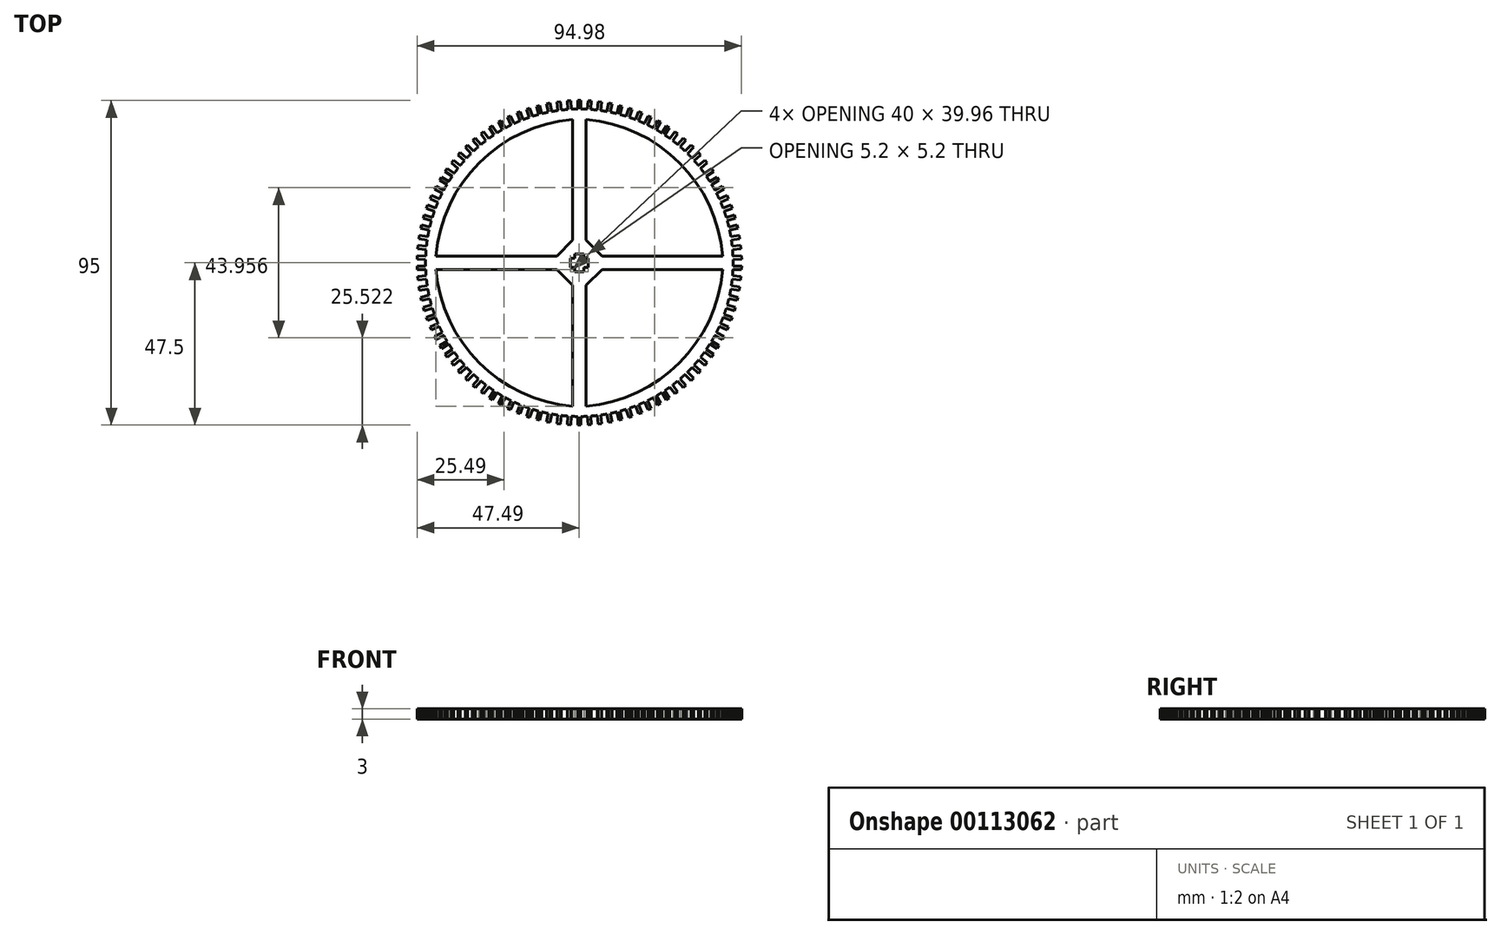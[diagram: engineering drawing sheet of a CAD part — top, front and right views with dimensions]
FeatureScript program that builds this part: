
annotation { "Feature Type Name" : "Feature", "Feature Type Description" : "" }
export const myFeature = defineFeature(function(context is Context, id is Id, definition is map)
    precondition{}
    {
        {
            var Q0;
            Q0=qCreatedBy(makeId("Top.planeOp"),FACE);
            var sketch = newSketch(context, id + "F0", { "sketchPlane" : qUnion([Q0])});
            skCircle(sketch, "E0", {"center": v(0, 0) * mm, "radius": 45 * mm});
            skLineSegment(sketch, "E1", {"start": v(0, 2.6) * mm, "end": v(1.3, 2.6) * mm});
            skLineSegment(sketch, "E2", {"start": v(1.3, 2.6) * mm, "end": v(1.3, 1.3) * mm});
            skLineSegment(sketch, "E3", {"start": v(1.3, 1.3) * mm, "end": v(2.6, 1.3) * mm});
            skLineSegment(sketch, "E4", {"start": v(2.6, 1.3) * mm, "end": v(2.6, 0) * mm});
            skLineSegment(sketch, "E5.MirrorCS", {"start": v(0, 2.6) * mm, "end": v(-1.3, 2.6) * mm});
            skLineSegment(sketch, "E6.MirrorCS", {"start": v(-1.3, 2.6) * mm, "end": v(-1.3, 1.3) * mm});
            skLineSegment(sketch, "E7.MirrorCS", {"start": v(-1.3, 1.3) * mm, "end": v(-2.6, 1.3) * mm});
            skLineSegment(sketch, "E8.MirrorCS", {"start": v(-2.6, 1.3) * mm, "end": v(-2.6, 0) * mm});
            skLineSegment(sketch, "E9", {"start": v(0, 45) * mm, "end": v(0, 47.5) * mm});
            skLineSegment(sketch, "E10", {"start": v(0, 47.5) * mm, "end": v(0.5, 47.5) * mm});
            skLineSegment(sketch, "E11", {"start": v(0.5, 47.5) * mm, "end": v(-0.5, 47.5) * mm});
            skLineSegment(sketch, "E12", {"start": v(-0.5, 47.5) * mm, "end": v(-0.5, 45) * mm});
            skLineSegment(sketch, "E13", {"start": v(0.5, 47.5) * mm, "end": v(0.5, 45) * mm});
            skLineSegment(sketch, "E14.1.0", {"start": v(-3.54, 47.37) * mm, "end": v(-3.38, 44.87) * mm});
            skLineSegment(sketch, "E14.1.1", {"start": v(-2.54, 47.43) * mm, "end": v(-3.54, 47.37) * mm});
            skLineSegment(sketch, "E14.1.2", {"start": v(-2.54, 47.43) * mm, "end": v(-2.38, 44.94) * mm});
            skLineSegment(sketch, "E14.2.0", {"start": v(-6.57, 47.05) * mm, "end": v(-6.25, 44.56) * mm});
            skLineSegment(sketch, "E14.2.1", {"start": v(-5.58, 47.17) * mm, "end": v(-6.57, 47.05) * mm});
            skLineSegment(sketch, "E14.2.2", {"start": v(-5.58, 47.17) * mm, "end": v(-5.26, 44.7) * mm});
            skLineSegment(sketch, "E15.2.3.0", {"start": v(-9.57, 46.53) * mm, "end": v(-9.1, 44.07) * mm});
            skLineSegment(sketch, "E15.3.3.0", {"start": v(-8.59, 46.72) * mm, "end": v(-9.57, 46.53) * mm});
            skLineSegment(sketch, "E15.6.3.0", {"start": v(-8.59, 46.72) * mm, "end": v(-8.11, 44.26) * mm});
            skLineSegment(sketch, "E15.2.4.0", {"start": v(-12.53, 45.82) * mm, "end": v(-11.9, 43.4) * mm});
            skLineSegment(sketch, "E15.3.4.0", {"start": v(-11.56, 46.07) * mm, "end": v(-12.53, 45.82) * mm});
            skLineSegment(sketch, "E15.6.4.0", {"start": v(-11.56, 46.07) * mm, "end": v(-10.93, 43.65) * mm});
            skLineSegment(sketch, "E15.2.5.0", {"start": v(-15.44, 44.92) * mm, "end": v(-14.65, 42.55) * mm});
            skLineSegment(sketch, "E15.3.5.0", {"start": v(-14.5, 45.24) * mm, "end": v(-15.44, 44.92) * mm});
            skLineSegment(sketch, "E15.6.5.0", {"start": v(-14.5, 45.24) * mm, "end": v(-13.7, 42.86) * mm});
            skLineSegment(sketch, "E15.2.6.0", {"start": v(-18.29, 43.84) * mm, "end": v(-17.35, 41.52) * mm});
            skLineSegment(sketch, "E15.3.6.0", {"start": v(-17.36, 44.22) * mm, "end": v(-18.29, 43.84) * mm});
            skLineSegment(sketch, "E15.6.6.0", {"start": v(-17.36, 44.22) * mm, "end": v(-16.42, 41.9) * mm});
            skLineSegment(sketch, "E15.2.7.0", {"start": v(-21.06, 42.58) * mm, "end": v(-19.97, 40.32) * mm});
            skLineSegment(sketch, "E15.3.7.0", {"start": v(-20.16, 43.01) * mm, "end": v(-21.06, 42.58) * mm});
            skLineSegment(sketch, "E15.6.7.0", {"start": v(-20.16, 43.01) * mm, "end": v(-19.07, 40.76) * mm});
            skLineSegment(sketch, "E15.2.8.0", {"start": v(-23.74, 41.14) * mm, "end": v(-22.52, 38.96) * mm});
            skLineSegment(sketch, "E15.3.8.0", {"start": v(-22.87, 41.63) * mm, "end": v(-23.74, 41.14) * mm});
            skLineSegment(sketch, "E15.6.8.0", {"start": v(-22.87, 41.63) * mm, "end": v(-21.65, 39.45) * mm});
            skLineSegment(sketch, "E15.2.9.0", {"start": v(-26.33, 39.54) * mm, "end": v(-24.97, 37.44) * mm});
            skLineSegment(sketch, "E15.3.9.0", {"start": v(-25.5, 40.08) * mm, "end": v(-26.33, 39.54) * mm});
            skLineSegment(sketch, "E15.6.9.0", {"start": v(-25.5, 40.08) * mm, "end": v(-24.13, 37.98) * mm});
            skLineSegment(sketch, "E15.2.10.0", {"start": v(-28.81, 37.77) * mm, "end": v(-27.31, 35.76) * mm});
            skLineSegment(sketch, "E15.3.10.0", {"start": v(-28, 38.37) * mm, "end": v(-28.81, 37.77) * mm});
            skLineSegment(sketch, "E15.6.10.0", {"start": v(-28, 38.37) * mm, "end": v(-26.51, 36.36) * mm});
            skLineSegment(sketch, "E15.2.11.0", {"start": v(-31.17, 35.84) * mm, "end": v(-29.55, 33.94) * mm});
            skLineSegment(sketch, "E15.3.11.0", {"start": v(-30.41, 36.5) * mm, "end": v(-31.17, 35.84) * mm});
            skLineSegment(sketch, "E15.6.11.0", {"start": v(-30.41, 36.5) * mm, "end": v(-28.79, 34.59) * mm});
            skLineSegment(sketch, "E15.2.12.0", {"start": v(-33.4, 33.77) * mm, "end": v(-31.66, 31.98) * mm});
            skLineSegment(sketch, "E15.3.12.0", {"start": v(-32.69, 34.47) * mm, "end": v(-33.4, 33.77) * mm});
            skLineSegment(sketch, "E15.6.12.0", {"start": v(-32.69, 34.47) * mm, "end": v(-30.94, 32.67) * mm});
            skLineSegment(sketch, "E15.2.13.0", {"start": v(-35.5, 31.56) * mm, "end": v(-33.65, 29.88) * mm});
            skLineSegment(sketch, "E15.3.13.0", {"start": v(-34.83, 32.3) * mm, "end": v(-35.5, 31.56) * mm});
            skLineSegment(sketch, "E15.6.13.0", {"start": v(-34.83, 32.3) * mm, "end": v(-32.97, 30.62) * mm});
            skLineSegment(sketch, "E15.2.14.0", {"start": v(-37.45, 29.22) * mm, "end": v(-35.5, 27.66) * mm});
            skLineSegment(sketch, "E15.3.14.0", {"start": v(-36.83, 30) * mm, "end": v(-37.45, 29.22) * mm});
            skLineSegment(sketch, "E15.6.14.0", {"start": v(-36.83, 30) * mm, "end": v(-34.87, 28.45) * mm});
            skLineSegment(sketch, "E15.2.15.0", {"start": v(-39.24, 26.77) * mm, "end": v(-37.2, 25.33) * mm});
            skLineSegment(sketch, "E15.3.15.0", {"start": v(-38.67, 27.59) * mm, "end": v(-39.24, 26.77) * mm});
            skLineSegment(sketch, "E15.6.15.0", {"start": v(-38.67, 27.59) * mm, "end": v(-36.62, 26.15) * mm});
            skLineSegment(sketch, "E15.2.16.0", {"start": v(-40.88, 24.2) * mm, "end": v(-38.74, 22.9) * mm});
            skLineSegment(sketch, "E15.3.16.0", {"start": v(-40.36, 25.05) * mm, "end": v(-40.88, 24.2) * mm});
            skLineSegment(sketch, "E15.6.16.0", {"start": v(-40.36, 25.05) * mm, "end": v(-38.22, 23.75) * mm});
            skLineSegment(sketch, "E15.2.17.0", {"start": v(-42.34, 21.53) * mm, "end": v(-40.13, 20.37) * mm});
            skLineSegment(sketch, "E15.3.17.0", {"start": v(-41.88, 22.41) * mm, "end": v(-42.34, 21.53) * mm});
            skLineSegment(sketch, "E15.6.17.0", {"start": v(-41.88, 22.41) * mm, "end": v(-39.66, 21.26) * mm});
            skLineSegment(sketch, "E15.2.18.0", {"start": v(-43.64, 18.77) * mm, "end": v(-41.35, 17.76) * mm});
            skLineSegment(sketch, "E15.3.18.0", {"start": v(-43.23, 19.68) * mm, "end": v(-43.64, 18.77) * mm});
            skLineSegment(sketch, "E15.6.18.0", {"start": v(-43.23, 19.68) * mm, "end": v(-40.94, 18.67) * mm});
            skLineSegment(sketch, "E15.2.19.0", {"start": v(-44.75, 15.94) * mm, "end": v(-42.4, 15.07) * mm});
            skLineSegment(sketch, "E15.3.19.0", {"start": v(-44.4, 16.87) * mm, "end": v(-44.75, 15.94) * mm});
            skLineSegment(sketch, "E15.6.19.0", {"start": v(-44.4, 16.87) * mm, "end": v(-42.06, 16) * mm});
            skLineSegment(sketch, "E15.2.20.0", {"start": v(-45.68, 13.04) * mm, "end": v(-43.28, 12.32) * mm});
            skLineSegment(sketch, "E15.3.20.0", {"start": v(-45.4, 14) * mm, "end": v(-45.68, 13.04) * mm});
            skLineSegment(sketch, "E15.6.20.0", {"start": v(-45.4, 14) * mm, "end": v(-43, 13.28) * mm});
            skLineSegment(sketch, "E15.2.21.0", {"start": v(-46.42, 10.08) * mm, "end": v(-43.98, 9.53) * mm});
            skLineSegment(sketch, "E15.3.21.0", {"start": v(-46.2, 11.06) * mm, "end": v(-46.42, 10.08) * mm});
            skLineSegment(sketch, "E15.6.21.0", {"start": v(-46.2, 11.06) * mm, "end": v(-43.76, 10.5) * mm});
            skLineSegment(sketch, "E15.2.22.0", {"start": v(-46.97, 7.09) * mm, "end": v(-44.5, 6.69) * mm});
            skLineSegment(sketch, "E15.3.22.0", {"start": v(-46.81, 8.07) * mm, "end": v(-46.97, 7.09) * mm});
            skLineSegment(sketch, "E15.6.22.0", {"start": v(-46.81, 8.07) * mm, "end": v(-44.34, 7.68) * mm});
            skLineSegment(sketch, "E15.2.23.0", {"start": v(-47.33, 4.06) * mm, "end": v(-44.84, 3.82) * mm});
            skLineSegment(sketch, "E15.3.23.0", {"start": v(-47.23, 5.06) * mm, "end": v(-47.33, 4.06) * mm});
            skLineSegment(sketch, "E15.6.23.0", {"start": v(-47.23, 5.06) * mm, "end": v(-44.74, 4.82) * mm});
            skLineSegment(sketch, "E15.2.24.0", {"start": v(-47.5, 1.02) * mm, "end": v(-45, 0.94) * mm});
            skLineSegment(sketch, "E15.3.24.0", {"start": v(-47.46, 2.02) * mm, "end": v(-47.5, 1.02) * mm});
            skLineSegment(sketch, "E15.6.24.0", {"start": v(-47.46, 2.02) * mm, "end": v(-44.96, 1.94) * mm});
            skLineSegment(sketch, "E15.2.25.0", {"start": v(-47.46, -2.02) * mm, "end": v(-44.96, -1.94) * mm});
            skLineSegment(sketch, "E15.3.25.0", {"start": v(-47.5, -1.02) * mm, "end": v(-47.46, -2.02) * mm});
            skLineSegment(sketch, "E15.6.25.0", {"start": v(-47.5, -1.02) * mm, "end": v(-45, -0.94) * mm});
            skLineSegment(sketch, "E15.2.26.0", {"start": v(-47.23, -5.06) * mm, "end": v(-44.74, -4.82) * mm});
            skLineSegment(sketch, "E15.3.26.0", {"start": v(-47.33, -4.06) * mm, "end": v(-47.23, -5.06) * mm});
            skLineSegment(sketch, "E15.6.26.0", {"start": v(-47.33, -4.06) * mm, "end": v(-44.84, -3.82) * mm});
            skLineSegment(sketch, "E15.2.27.0", {"start": v(-46.81, -8.07) * mm, "end": v(-44.34, -7.68) * mm});
            skLineSegment(sketch, "E15.3.27.0", {"start": v(-46.97, -7.09) * mm, "end": v(-46.81, -8.07) * mm});
            skLineSegment(sketch, "E15.6.27.0", {"start": v(-46.97, -7.09) * mm, "end": v(-44.5, -6.69) * mm});
            skLineSegment(sketch, "E15.2.28.0", {"start": v(-46.2, -11.06) * mm, "end": v(-43.76, -10.5) * mm});
            skLineSegment(sketch, "E15.3.28.0", {"start": v(-46.42, -10.08) * mm, "end": v(-46.2, -11.06) * mm});
            skLineSegment(sketch, "E15.6.28.0", {"start": v(-46.42, -10.08) * mm, "end": v(-43.98, -9.53) * mm});
            skLineSegment(sketch, "E15.2.29.0", {"start": v(-45.4, -14) * mm, "end": v(-43, -13.28) * mm});
            skLineSegment(sketch, "E15.3.29.0", {"start": v(-45.68, -13.04) * mm, "end": v(-45.4, -14) * mm});
            skLineSegment(sketch, "E15.6.29.0", {"start": v(-45.68, -13.04) * mm, "end": v(-43.28, -12.32) * mm});
            skLineSegment(sketch, "E15.2.30.0", {"start": v(-44.4, -16.87) * mm, "end": v(-42.06, -16) * mm});
            skLineSegment(sketch, "E15.3.30.0", {"start": v(-44.75, -15.94) * mm, "end": v(-44.4, -16.87) * mm});
            skLineSegment(sketch, "E15.6.30.0", {"start": v(-44.75, -15.94) * mm, "end": v(-42.4, -15.07) * mm});
            skLineSegment(sketch, "E15.2.31.0", {"start": v(-43.23, -19.68) * mm, "end": v(-40.94, -18.67) * mm});
            skLineSegment(sketch, "E15.3.31.0", {"start": v(-43.64, -18.77) * mm, "end": v(-43.23, -19.68) * mm});
            skLineSegment(sketch, "E15.6.31.0", {"start": v(-43.64, -18.77) * mm, "end": v(-41.35, -17.76) * mm});
            skLineSegment(sketch, "E15.2.32.0", {"start": v(-41.88, -22.41) * mm, "end": v(-39.66, -21.26) * mm});
            skLineSegment(sketch, "E15.3.32.0", {"start": v(-42.34, -21.53) * mm, "end": v(-41.88, -22.41) * mm});
            skLineSegment(sketch, "E15.6.32.0", {"start": v(-42.34, -21.53) * mm, "end": v(-40.13, -20.37) * mm});
            skLineSegment(sketch, "E15.2.33.0", {"start": v(-40.36, -25.05) * mm, "end": v(-38.22, -23.75) * mm});
            skLineSegment(sketch, "E15.3.33.0", {"start": v(-40.88, -24.2) * mm, "end": v(-40.36, -25.05) * mm});
            skLineSegment(sketch, "E15.6.33.0", {"start": v(-40.88, -24.2) * mm, "end": v(-38.74, -22.9) * mm});
            skLineSegment(sketch, "E15.2.34.0", {"start": v(-38.67, -27.59) * mm, "end": v(-36.62, -26.15) * mm});
            skLineSegment(sketch, "E15.3.34.0", {"start": v(-39.24, -26.77) * mm, "end": v(-38.67, -27.59) * mm});
            skLineSegment(sketch, "E15.6.34.0", {"start": v(-39.24, -26.77) * mm, "end": v(-37.2, -25.33) * mm});
            skLineSegment(sketch, "E15.2.35.0", {"start": v(-36.83, -30) * mm, "end": v(-34.87, -28.45) * mm});
            skLineSegment(sketch, "E15.3.35.0", {"start": v(-37.45, -29.22) * mm, "end": v(-36.83, -30) * mm});
            skLineSegment(sketch, "E15.6.35.0", {"start": v(-37.45, -29.22) * mm, "end": v(-35.5, -27.66) * mm});
            skLineSegment(sketch, "E15.2.36.0", {"start": v(-34.83, -32.3) * mm, "end": v(-32.97, -30.62) * mm});
            skLineSegment(sketch, "E15.3.36.0", {"start": v(-35.5, -31.56) * mm, "end": v(-34.83, -32.3) * mm});
            skLineSegment(sketch, "E15.6.36.0", {"start": v(-35.5, -31.56) * mm, "end": v(-33.65, -29.88) * mm});
            skLineSegment(sketch, "E15.2.37.0", {"start": v(-32.69, -34.47) * mm, "end": v(-30.94, -32.67) * mm});
            skLineSegment(sketch, "E15.3.37.0", {"start": v(-33.4, -33.77) * mm, "end": v(-32.69, -34.47) * mm});
            skLineSegment(sketch, "E15.6.37.0", {"start": v(-33.4, -33.77) * mm, "end": v(-31.66, -31.98) * mm});
            skLineSegment(sketch, "E15.2.38.0", {"start": v(-30.41, -36.5) * mm, "end": v(-28.79, -34.59) * mm});
            skLineSegment(sketch, "E15.3.38.0", {"start": v(-31.17, -35.84) * mm, "end": v(-30.41, -36.5) * mm});
            skLineSegment(sketch, "E15.6.38.0", {"start": v(-31.17, -35.84) * mm, "end": v(-29.55, -33.94) * mm});
            skLineSegment(sketch, "E15.2.39.0", {"start": v(-28, -38.37) * mm, "end": v(-26.51, -36.36) * mm});
            skLineSegment(sketch, "E15.3.39.0", {"start": v(-28.81, -37.77) * mm, "end": v(-28, -38.37) * mm});
            skLineSegment(sketch, "E15.6.39.0", {"start": v(-28.81, -37.77) * mm, "end": v(-27.31, -35.76) * mm});
            skLineSegment(sketch, "E15.2.40.0", {"start": v(-25.5, -40.08) * mm, "end": v(-24.13, -37.98) * mm});
            skLineSegment(sketch, "E15.3.40.0", {"start": v(-26.33, -39.54) * mm, "end": v(-25.5, -40.08) * mm});
            skLineSegment(sketch, "E15.6.40.0", {"start": v(-26.33, -39.54) * mm, "end": v(-24.97, -37.44) * mm});
            skLineSegment(sketch, "E15.2.41.0", {"start": v(-22.87, -41.63) * mm, "end": v(-21.65, -39.45) * mm});
            skLineSegment(sketch, "E15.3.41.0", {"start": v(-23.74, -41.14) * mm, "end": v(-22.87, -41.63) * mm});
            skLineSegment(sketch, "E15.6.41.0", {"start": v(-23.74, -41.14) * mm, "end": v(-22.52, -38.96) * mm});
            skLineSegment(sketch, "E15.2.42.0", {"start": v(-20.16, -43.01) * mm, "end": v(-19.07, -40.76) * mm});
            skLineSegment(sketch, "E15.3.42.0", {"start": v(-21.06, -42.58) * mm, "end": v(-20.16, -43.01) * mm});
            skLineSegment(sketch, "E15.6.42.0", {"start": v(-21.06, -42.58) * mm, "end": v(-19.97, -40.32) * mm});
            skLineSegment(sketch, "E15.2.43.0", {"start": v(-17.36, -44.22) * mm, "end": v(-16.42, -41.9) * mm});
            skLineSegment(sketch, "E15.3.43.0", {"start": v(-18.29, -43.84) * mm, "end": v(-17.36, -44.22) * mm});
            skLineSegment(sketch, "E15.6.43.0", {"start": v(-18.29, -43.84) * mm, "end": v(-17.35, -41.52) * mm});
            skLineSegment(sketch, "E15.2.44.0", {"start": v(-14.5, -45.24) * mm, "end": v(-13.7, -42.86) * mm});
            skLineSegment(sketch, "E15.3.44.0", {"start": v(-15.44, -44.92) * mm, "end": v(-14.5, -45.24) * mm});
            skLineSegment(sketch, "E15.6.44.0", {"start": v(-15.44, -44.92) * mm, "end": v(-14.65, -42.55) * mm});
            skLineSegment(sketch, "E15.2.45.0", {"start": v(-11.56, -46.07) * mm, "end": v(-10.93, -43.65) * mm});
            skLineSegment(sketch, "E15.3.45.0", {"start": v(-12.53, -45.82) * mm, "end": v(-11.56, -46.07) * mm});
            skLineSegment(sketch, "E15.6.45.0", {"start": v(-12.53, -45.82) * mm, "end": v(-11.9, -43.4) * mm});
            skLineSegment(sketch, "E15.2.46.0", {"start": v(-8.59, -46.72) * mm, "end": v(-8.11, -44.26) * mm});
            skLineSegment(sketch, "E15.3.46.0", {"start": v(-9.57, -46.53) * mm, "end": v(-8.59, -46.72) * mm});
            skLineSegment(sketch, "E15.6.46.0", {"start": v(-9.57, -46.53) * mm, "end": v(-9.1, -44.07) * mm});
            skLineSegment(sketch, "E15.2.47.0", {"start": v(-5.58, -47.17) * mm, "end": v(-5.26, -44.7) * mm});
            skLineSegment(sketch, "E15.3.47.0", {"start": v(-6.57, -47.05) * mm, "end": v(-5.58, -47.17) * mm});
            skLineSegment(sketch, "E15.6.47.0", {"start": v(-6.57, -47.05) * mm, "end": v(-6.25, -44.56) * mm});
            skLineSegment(sketch, "E15.2.48.0", {"start": v(-2.54, -47.43) * mm, "end": v(-2.38, -44.94) * mm});
            skLineSegment(sketch, "E15.3.48.0", {"start": v(-3.54, -47.37) * mm, "end": v(-2.54, -47.43) * mm});
            skLineSegment(sketch, "E15.6.48.0", {"start": v(-3.54, -47.37) * mm, "end": v(-3.38, -44.87) * mm});
            skLineSegment(sketch, "E15.2.49.0", {"start": v(0.5, -47.5) * mm, "end": v(0.5, -45) * mm});
            skLineSegment(sketch, "E15.3.49.0", {"start": v(-0.5, -47.5) * mm, "end": v(0.5, -47.5) * mm});
            skLineSegment(sketch, "E15.6.49.0", {"start": v(-0.5, -47.5) * mm, "end": v(-0.5, -45) * mm});
            skLineSegment(sketch, "E15.2.50.0", {"start": v(3.54, -47.37) * mm, "end": v(3.38, -44.87) * mm});
            skLineSegment(sketch, "E15.3.50.0", {"start": v(2.54, -47.43) * mm, "end": v(3.54, -47.37) * mm});
            skLineSegment(sketch, "E15.6.50.0", {"start": v(2.54, -47.43) * mm, "end": v(2.38, -44.94) * mm});
            skLineSegment(sketch, "E15.2.51.0", {"start": v(6.57, -47.05) * mm, "end": v(6.25, -44.56) * mm});
            skLineSegment(sketch, "E15.3.51.0", {"start": v(5.58, -47.17) * mm, "end": v(6.57, -47.05) * mm});
            skLineSegment(sketch, "E15.6.51.0", {"start": v(5.58, -47.17) * mm, "end": v(5.26, -44.7) * mm});
            skLineSegment(sketch, "E15.2.52.0", {"start": v(9.57, -46.53) * mm, "end": v(9.1, -44.07) * mm});
            skLineSegment(sketch, "E15.3.52.0", {"start": v(8.59, -46.72) * mm, "end": v(9.57, -46.53) * mm});
            skLineSegment(sketch, "E15.6.52.0", {"start": v(8.59, -46.72) * mm, "end": v(8.11, -44.26) * mm});
            skLineSegment(sketch, "E15.2.53.0", {"start": v(12.53, -45.82) * mm, "end": v(11.9, -43.4) * mm});
            skLineSegment(sketch, "E15.3.53.0", {"start": v(11.56, -46.07) * mm, "end": v(12.53, -45.82) * mm});
            skLineSegment(sketch, "E15.6.53.0", {"start": v(11.56, -46.07) * mm, "end": v(10.93, -43.65) * mm});
            skLineSegment(sketch, "E15.2.54.0", {"start": v(15.44, -44.92) * mm, "end": v(14.65, -42.55) * mm});
            skLineSegment(sketch, "E15.3.54.0", {"start": v(14.5, -45.24) * mm, "end": v(15.44, -44.92) * mm});
            skLineSegment(sketch, "E15.6.54.0", {"start": v(14.5, -45.24) * mm, "end": v(13.7, -42.86) * mm});
            skLineSegment(sketch, "E15.2.55.0", {"start": v(18.29, -43.84) * mm, "end": v(17.35, -41.52) * mm});
            skLineSegment(sketch, "E15.3.55.0", {"start": v(17.36, -44.22) * mm, "end": v(18.29, -43.84) * mm});
            skLineSegment(sketch, "E15.6.55.0", {"start": v(17.36, -44.22) * mm, "end": v(16.42, -41.9) * mm});
            skLineSegment(sketch, "E15.2.56.0", {"start": v(21.06, -42.58) * mm, "end": v(19.97, -40.32) * mm});
            skLineSegment(sketch, "E15.3.56.0", {"start": v(20.16, -43.01) * mm, "end": v(21.06, -42.58) * mm});
            skLineSegment(sketch, "E15.6.56.0", {"start": v(20.16, -43.01) * mm, "end": v(19.07, -40.76) * mm});
            skLineSegment(sketch, "E15.2.57.0", {"start": v(23.74, -41.14) * mm, "end": v(22.52, -38.96) * mm});
            skLineSegment(sketch, "E15.3.57.0", {"start": v(22.87, -41.63) * mm, "end": v(23.74, -41.14) * mm});
            skLineSegment(sketch, "E15.6.57.0", {"start": v(22.87, -41.63) * mm, "end": v(21.65, -39.45) * mm});
            skLineSegment(sketch, "E15.2.58.0", {"start": v(26.33, -39.54) * mm, "end": v(24.97, -37.44) * mm});
            skLineSegment(sketch, "E15.3.58.0", {"start": v(25.5, -40.08) * mm, "end": v(26.33, -39.54) * mm});
            skLineSegment(sketch, "E15.6.58.0", {"start": v(25.5, -40.08) * mm, "end": v(24.13, -37.98) * mm});
            skLineSegment(sketch, "E15.2.59.0", {"start": v(28.81, -37.77) * mm, "end": v(27.31, -35.76) * mm});
            skLineSegment(sketch, "E15.3.59.0", {"start": v(28, -38.37) * mm, "end": v(28.81, -37.77) * mm});
            skLineSegment(sketch, "E15.6.59.0", {"start": v(28, -38.37) * mm, "end": v(26.51, -36.36) * mm});
            skLineSegment(sketch, "E15.2.60.0", {"start": v(31.17, -35.84) * mm, "end": v(29.55, -33.94) * mm});
            skLineSegment(sketch, "E15.3.60.0", {"start": v(30.41, -36.5) * mm, "end": v(31.17, -35.84) * mm});
            skLineSegment(sketch, "E15.6.60.0", {"start": v(30.41, -36.5) * mm, "end": v(28.79, -34.59) * mm});
            skLineSegment(sketch, "E15.2.61.0", {"start": v(33.4, -33.77) * mm, "end": v(31.66, -31.98) * mm});
            skLineSegment(sketch, "E15.3.61.0", {"start": v(32.69, -34.47) * mm, "end": v(33.4, -33.77) * mm});
            skLineSegment(sketch, "E15.6.61.0", {"start": v(32.69, -34.47) * mm, "end": v(30.94, -32.67) * mm});
            skLineSegment(sketch, "E15.2.62.0", {"start": v(35.5, -31.56) * mm, "end": v(33.65, -29.88) * mm});
            skLineSegment(sketch, "E15.3.62.0", {"start": v(34.83, -32.3) * mm, "end": v(35.5, -31.56) * mm});
            skLineSegment(sketch, "E15.6.62.0", {"start": v(34.83, -32.3) * mm, "end": v(32.97, -30.62) * mm});
            skLineSegment(sketch, "E15.2.63.0", {"start": v(37.45, -29.22) * mm, "end": v(35.5, -27.66) * mm});
            skLineSegment(sketch, "E15.3.63.0", {"start": v(36.83, -30) * mm, "end": v(37.45, -29.22) * mm});
            skLineSegment(sketch, "E15.6.63.0", {"start": v(36.83, -30) * mm, "end": v(34.87, -28.45) * mm});
            skLineSegment(sketch, "E15.2.64.0", {"start": v(39.24, -26.77) * mm, "end": v(37.2, -25.33) * mm});
            skLineSegment(sketch, "E15.3.64.0", {"start": v(38.67, -27.59) * mm, "end": v(39.24, -26.77) * mm});
            skLineSegment(sketch, "E15.6.64.0", {"start": v(38.67, -27.59) * mm, "end": v(36.62, -26.15) * mm});
            skLineSegment(sketch, "E15.2.65.0", {"start": v(40.88, -24.2) * mm, "end": v(38.74, -22.9) * mm});
            skLineSegment(sketch, "E15.3.65.0", {"start": v(40.36, -25.05) * mm, "end": v(40.88, -24.2) * mm});
            skLineSegment(sketch, "E15.6.65.0", {"start": v(40.36, -25.05) * mm, "end": v(38.22, -23.75) * mm});
            skLineSegment(sketch, "E15.2.66.0", {"start": v(42.34, -21.53) * mm, "end": v(40.13, -20.37) * mm});
            skLineSegment(sketch, "E15.3.66.0", {"start": v(41.88, -22.41) * mm, "end": v(42.34, -21.53) * mm});
            skLineSegment(sketch, "E15.6.66.0", {"start": v(41.88, -22.41) * mm, "end": v(39.66, -21.26) * mm});
            skLineSegment(sketch, "E15.2.67.0", {"start": v(43.64, -18.77) * mm, "end": v(41.35, -17.76) * mm});
            skLineSegment(sketch, "E15.3.67.0", {"start": v(43.23, -19.68) * mm, "end": v(43.64, -18.77) * mm});
            skLineSegment(sketch, "E15.6.67.0", {"start": v(43.23, -19.68) * mm, "end": v(40.94, -18.67) * mm});
            skLineSegment(sketch, "E15.2.68.0", {"start": v(44.75, -15.94) * mm, "end": v(42.4, -15.07) * mm});
            skLineSegment(sketch, "E15.3.68.0", {"start": v(44.4, -16.87) * mm, "end": v(44.75, -15.94) * mm});
            skLineSegment(sketch, "E15.6.68.0", {"start": v(44.4, -16.87) * mm, "end": v(42.06, -16) * mm});
            skLineSegment(sketch, "E15.2.69.0", {"start": v(45.68, -13.04) * mm, "end": v(43.28, -12.32) * mm});
            skLineSegment(sketch, "E15.3.69.0", {"start": v(45.4, -14) * mm, "end": v(45.68, -13.04) * mm});
            skLineSegment(sketch, "E15.6.69.0", {"start": v(45.4, -14) * mm, "end": v(43, -13.28) * mm});
            skLineSegment(sketch, "E15.2.70.0", {"start": v(46.42, -10.08) * mm, "end": v(43.98, -9.53) * mm});
            skLineSegment(sketch, "E15.3.70.0", {"start": v(46.2, -11.06) * mm, "end": v(46.42, -10.08) * mm});
            skLineSegment(sketch, "E15.6.70.0", {"start": v(46.2, -11.06) * mm, "end": v(43.76, -10.5) * mm});
            skLineSegment(sketch, "E15.2.71.0", {"start": v(46.97, -7.09) * mm, "end": v(44.5, -6.69) * mm});
            skLineSegment(sketch, "E15.3.71.0", {"start": v(46.81, -8.07) * mm, "end": v(46.97, -7.09) * mm});
            skLineSegment(sketch, "E15.6.71.0", {"start": v(46.81, -8.07) * mm, "end": v(44.34, -7.68) * mm});
            skLineSegment(sketch, "E15.2.72.0", {"start": v(47.33, -4.06) * mm, "end": v(44.84, -3.82) * mm});
            skLineSegment(sketch, "E15.3.72.0", {"start": v(47.23, -5.06) * mm, "end": v(47.33, -4.06) * mm});
            skLineSegment(sketch, "E15.6.72.0", {"start": v(47.23, -5.06) * mm, "end": v(44.74, -4.82) * mm});
            skLineSegment(sketch, "E15.2.73.0", {"start": v(47.5, -1.02) * mm, "end": v(45, -0.94) * mm});
            skLineSegment(sketch, "E15.3.73.0", {"start": v(47.46, -2.02) * mm, "end": v(47.5, -1.02) * mm});
            skLineSegment(sketch, "E15.6.73.0", {"start": v(47.46, -2.02) * mm, "end": v(44.96, -1.94) * mm});
            skLineSegment(sketch, "E15.2.74.0", {"start": v(47.46, 2.02) * mm, "end": v(44.96, 1.94) * mm});
            skLineSegment(sketch, "E15.3.74.0", {"start": v(47.5, 1.02) * mm, "end": v(47.46, 2.02) * mm});
            skLineSegment(sketch, "E15.6.74.0", {"start": v(47.5, 1.02) * mm, "end": v(45, 0.94) * mm});
            skLineSegment(sketch, "E15.2.75.0", {"start": v(47.23, 5.06) * mm, "end": v(44.74, 4.82) * mm});
            skLineSegment(sketch, "E15.3.75.0", {"start": v(47.33, 4.06) * mm, "end": v(47.23, 5.06) * mm});
            skLineSegment(sketch, "E15.6.75.0", {"start": v(47.33, 4.06) * mm, "end": v(44.84, 3.82) * mm});
            skLineSegment(sketch, "E15.2.76.0", {"start": v(46.81, 8.07) * mm, "end": v(44.34, 7.68) * mm});
            skLineSegment(sketch, "E15.3.76.0", {"start": v(46.97, 7.09) * mm, "end": v(46.81, 8.07) * mm});
            skLineSegment(sketch, "E15.6.76.0", {"start": v(46.97, 7.09) * mm, "end": v(44.5, 6.69) * mm});
            skLineSegment(sketch, "E15.2.77.0", {"start": v(46.2, 11.06) * mm, "end": v(43.76, 10.5) * mm});
            skLineSegment(sketch, "E15.3.77.0", {"start": v(46.42, 10.08) * mm, "end": v(46.2, 11.06) * mm});
            skLineSegment(sketch, "E15.6.77.0", {"start": v(46.42, 10.08) * mm, "end": v(43.98, 9.53) * mm});
            skLineSegment(sketch, "E15.2.78.0", {"start": v(45.4, 14) * mm, "end": v(43, 13.28) * mm});
            skLineSegment(sketch, "E15.3.78.0", {"start": v(45.68, 13.04) * mm, "end": v(45.4, 14) * mm});
            skLineSegment(sketch, "E15.6.78.0", {"start": v(45.68, 13.04) * mm, "end": v(43.28, 12.32) * mm});
            skLineSegment(sketch, "E15.2.79.0", {"start": v(44.4, 16.87) * mm, "end": v(42.06, 16) * mm});
            skLineSegment(sketch, "E15.3.79.0", {"start": v(44.75, 15.94) * mm, "end": v(44.4, 16.87) * mm});
            skLineSegment(sketch, "E15.6.79.0", {"start": v(44.75, 15.94) * mm, "end": v(42.4, 15.07) * mm});
            skLineSegment(sketch, "E15.2.80.0", {"start": v(43.23, 19.68) * mm, "end": v(40.94, 18.67) * mm});
            skLineSegment(sketch, "E15.3.80.0", {"start": v(43.64, 18.77) * mm, "end": v(43.23, 19.68) * mm});
            skLineSegment(sketch, "E15.6.80.0", {"start": v(43.64, 18.77) * mm, "end": v(41.35, 17.76) * mm});
            skLineSegment(sketch, "E15.2.81.0", {"start": v(41.88, 22.41) * mm, "end": v(39.66, 21.26) * mm});
            skLineSegment(sketch, "E15.3.81.0", {"start": v(42.34, 21.53) * mm, "end": v(41.88, 22.41) * mm});
            skLineSegment(sketch, "E15.6.81.0", {"start": v(42.34, 21.53) * mm, "end": v(40.13, 20.37) * mm});
            skLineSegment(sketch, "E15.2.82.0", {"start": v(40.36, 25.05) * mm, "end": v(38.22, 23.75) * mm});
            skLineSegment(sketch, "E15.3.82.0", {"start": v(40.88, 24.2) * mm, "end": v(40.36, 25.05) * mm});
            skLineSegment(sketch, "E15.6.82.0", {"start": v(40.88, 24.2) * mm, "end": v(38.74, 22.9) * mm});
            skLineSegment(sketch, "E15.2.83.0", {"start": v(38.67, 27.59) * mm, "end": v(36.62, 26.15) * mm});
            skLineSegment(sketch, "E15.3.83.0", {"start": v(39.24, 26.77) * mm, "end": v(38.67, 27.59) * mm});
            skLineSegment(sketch, "E15.6.83.0", {"start": v(39.24, 26.77) * mm, "end": v(37.2, 25.33) * mm});
            skLineSegment(sketch, "E15.2.84.0", {"start": v(36.83, 30) * mm, "end": v(34.87, 28.45) * mm});
            skLineSegment(sketch, "E15.3.84.0", {"start": v(37.45, 29.22) * mm, "end": v(36.83, 30) * mm});
            skLineSegment(sketch, "E15.6.84.0", {"start": v(37.45, 29.22) * mm, "end": v(35.5, 27.66) * mm});
            skLineSegment(sketch, "E15.2.85.0", {"start": v(34.83, 32.3) * mm, "end": v(32.97, 30.62) * mm});
            skLineSegment(sketch, "E15.3.85.0", {"start": v(35.5, 31.56) * mm, "end": v(34.83, 32.3) * mm});
            skLineSegment(sketch, "E15.6.85.0", {"start": v(35.5, 31.56) * mm, "end": v(33.65, 29.88) * mm});
            skLineSegment(sketch, "E15.2.86.0", {"start": v(32.69, 34.47) * mm, "end": v(30.94, 32.67) * mm});
            skLineSegment(sketch, "E15.3.86.0", {"start": v(33.4, 33.77) * mm, "end": v(32.69, 34.47) * mm});
            skLineSegment(sketch, "E15.6.86.0", {"start": v(33.4, 33.77) * mm, "end": v(31.66, 31.98) * mm});
            skLineSegment(sketch, "E15.2.87.0", {"start": v(30.41, 36.5) * mm, "end": v(28.79, 34.59) * mm});
            skLineSegment(sketch, "E15.3.87.0", {"start": v(31.17, 35.84) * mm, "end": v(30.41, 36.5) * mm});
            skLineSegment(sketch, "E15.6.87.0", {"start": v(31.17, 35.84) * mm, "end": v(29.55, 33.94) * mm});
            skLineSegment(sketch, "E15.2.88.0", {"start": v(28, 38.37) * mm, "end": v(26.51, 36.36) * mm});
            skLineSegment(sketch, "E15.3.88.0", {"start": v(28.81, 37.77) * mm, "end": v(28, 38.37) * mm});
            skLineSegment(sketch, "E15.6.88.0", {"start": v(28.81, 37.77) * mm, "end": v(27.31, 35.76) * mm});
            skLineSegment(sketch, "E15.2.89.0", {"start": v(25.5, 40.08) * mm, "end": v(24.13, 37.98) * mm});
            skLineSegment(sketch, "E15.3.89.0", {"start": v(26.33, 39.54) * mm, "end": v(25.5, 40.08) * mm});
            skLineSegment(sketch, "E15.6.89.0", {"start": v(26.33, 39.54) * mm, "end": v(24.97, 37.44) * mm});
            skLineSegment(sketch, "E15.2.90.0", {"start": v(22.87, 41.63) * mm, "end": v(21.65, 39.45) * mm});
            skLineSegment(sketch, "E15.3.90.0", {"start": v(23.74, 41.14) * mm, "end": v(22.87, 41.63) * mm});
            skLineSegment(sketch, "E15.6.90.0", {"start": v(23.74, 41.14) * mm, "end": v(22.52, 38.96) * mm});
            skLineSegment(sketch, "E15.2.91.0", {"start": v(20.16, 43.01) * mm, "end": v(19.07, 40.76) * mm});
            skLineSegment(sketch, "E15.3.91.0", {"start": v(21.06, 42.58) * mm, "end": v(20.16, 43.01) * mm});
            skLineSegment(sketch, "E15.6.91.0", {"start": v(21.06, 42.58) * mm, "end": v(19.97, 40.32) * mm});
            skLineSegment(sketch, "E15.2.92.0", {"start": v(17.36, 44.22) * mm, "end": v(16.42, 41.9) * mm});
            skLineSegment(sketch, "E15.3.92.0", {"start": v(18.29, 43.84) * mm, "end": v(17.36, 44.22) * mm});
            skLineSegment(sketch, "E15.6.92.0", {"start": v(18.29, 43.84) * mm, "end": v(17.35, 41.52) * mm});
            skLineSegment(sketch, "E15.2.93.0", {"start": v(14.5, 45.24) * mm, "end": v(13.7, 42.86) * mm});
            skLineSegment(sketch, "E15.3.93.0", {"start": v(15.44, 44.92) * mm, "end": v(14.5, 45.24) * mm});
            skLineSegment(sketch, "E15.6.93.0", {"start": v(15.44, 44.92) * mm, "end": v(14.65, 42.55) * mm});
            skLineSegment(sketch, "E15.2.94.0", {"start": v(11.56, 46.07) * mm, "end": v(10.93, 43.65) * mm});
            skLineSegment(sketch, "E15.3.94.0", {"start": v(12.53, 45.82) * mm, "end": v(11.56, 46.07) * mm});
            skLineSegment(sketch, "E15.6.94.0", {"start": v(12.53, 45.82) * mm, "end": v(11.9, 43.4) * mm});
            skLineSegment(sketch, "E15.2.95.0", {"start": v(8.59, 46.72) * mm, "end": v(8.11, 44.26) * mm});
            skLineSegment(sketch, "E15.3.95.0", {"start": v(9.57, 46.53) * mm, "end": v(8.59, 46.72) * mm});
            skLineSegment(sketch, "E15.6.95.0", {"start": v(9.57, 46.53) * mm, "end": v(9.1, 44.07) * mm});
            skLineSegment(sketch, "E15.2.96.0", {"start": v(5.58, 47.17) * mm, "end": v(5.26, 44.7) * mm});
            skLineSegment(sketch, "E15.3.96.0", {"start": v(6.57, 47.05) * mm, "end": v(5.58, 47.17) * mm});
            skLineSegment(sketch, "E15.6.96.0", {"start": v(6.57, 47.05) * mm, "end": v(6.25, 44.56) * mm});
            skLineSegment(sketch, "E15.2.97.0", {"start": v(2.54, 47.43) * mm, "end": v(2.38, 44.94) * mm});
            skLineSegment(sketch, "E15.3.97.0", {"start": v(3.54, 47.37) * mm, "end": v(2.54, 47.43) * mm});
            skLineSegment(sketch, "E15.6.97.0", {"start": v(3.54, 47.37) * mm, "end": v(3.38, 44.87) * mm});
            skPoint(sketch, "E16.start.orphan", {"position": v(0, 39.95) * mm});
            skLineSegment(sketch, "E17", {"start": v(-2, 41.96) * mm, "end": v(-2, 6.6) * mm});
            skLineSegment(sketch, "E18", {"start": v(-42, 2) * mm, "end": v(-6.6, 2) * mm});
            skLineSegment(sketch, "E19", {"start": v(-6.6, 2) * mm, "end": v(-2, 6.6) * mm});
            skArc(sketch, "E20", {"start": v(-2, 41.96) * mm, "mid": v(-29.3, 29.28) * mm, "end": v(-42, 2) * mm});
            skPoint(sketch, "E21.start.orphan", {"position": v(-45, 0) * mm});
            skLineSegment(sketch, "E22.MirrorCS", {"start": v(2, 41.96) * mm, "end": v(2, 6.6) * mm});
            skArc(sketch, "E23.MirrorCS", {"start": v(2, 41.96) * mm, "mid": v(29.3, 29.28) * mm, "end": v(42, 2) * mm});
            skLineSegment(sketch, "E24.MirrorCS", {"start": v(42, 2) * mm, "end": v(6.6, 2) * mm});
            skLineSegment(sketch, "E25.MirrorCS", {"start": v(6.6, 2) * mm, "end": v(2, 6.6) * mm});
            skLineSegment(sketch, "E26.MirrorCS", {"start": v(-42, -2) * mm, "end": v(-6.6, -2) * mm});
            skLineSegment(sketch, "E27.MirrorCS", {"start": v(-6.6, -2) * mm, "end": v(-2, -6.6) * mm});
            skLineSegment(sketch, "E28.MirrorCS", {"start": v(-2, -41.96) * mm, "end": v(-2, -6.6) * mm});
            skArc(sketch, "E29.MirrorCS", {"start": v(-2, -41.96) * mm, "mid": v(-29.3, -29.28) * mm, "end": v(-42, -2) * mm});
            skLineSegment(sketch, "E30.MirrorCS", {"start": v(2, -41.96) * mm, "end": v(2, -6.6) * mm});
            skLineSegment(sketch, "E31.MirrorCS", {"start": v(6.6, -2) * mm, "end": v(2, -6.6) * mm});
            skLineSegment(sketch, "E32.MirrorCS", {"start": v(42, -2) * mm, "end": v(6.6, -2) * mm});
            skArc(sketch, "E33.MirrorCS", {"start": v(2, -41.96) * mm, "mid": v(29.3, -29.28) * mm, "end": v(42, -2) * mm});
            skLineSegment(sketch, "E34.MirrorCS", {"start": v(2.6, -1.3) * mm, "end": v(2.6, 0) * mm});
            skLineSegment(sketch, "E35.MirrorCS", {"start": v(1.3, -1.3) * mm, "end": v(2.6, -1.3) * mm});
            skLineSegment(sketch, "E36.MirrorCS", {"start": v(1.3, -2.6) * mm, "end": v(1.3, -1.3) * mm});
            skLineSegment(sketch, "E37.MirrorCS", {"start": v(0, -2.6) * mm, "end": v(1.3, -2.6) * mm});
            skLineSegment(sketch, "E38.MirrorCS", {"start": v(0, -2.6) * mm, "end": v(-1.3, -2.6) * mm});
            skLineSegment(sketch, "E39.MirrorCS", {"start": v(-1.3, -2.6) * mm, "end": v(-1.3, -1.3) * mm});
            skLineSegment(sketch, "E40.MirrorCS", {"start": v(-1.3, -1.3) * mm, "end": v(-2.6, -1.3) * mm});
            skLineSegment(sketch, "E41.MirrorCS", {"start": v(-2.6, -1.3) * mm, "end": v(-2.6, 0) * mm});
            skSolve(sketch);
        }
        {
            var Q0;
            Q0 = qSketchRegion(id + "F0", true);
            extrude(context, id + "F1", {"entities" : qUnion([Q0]), "depth" : 3 * mm});
        }
    });
